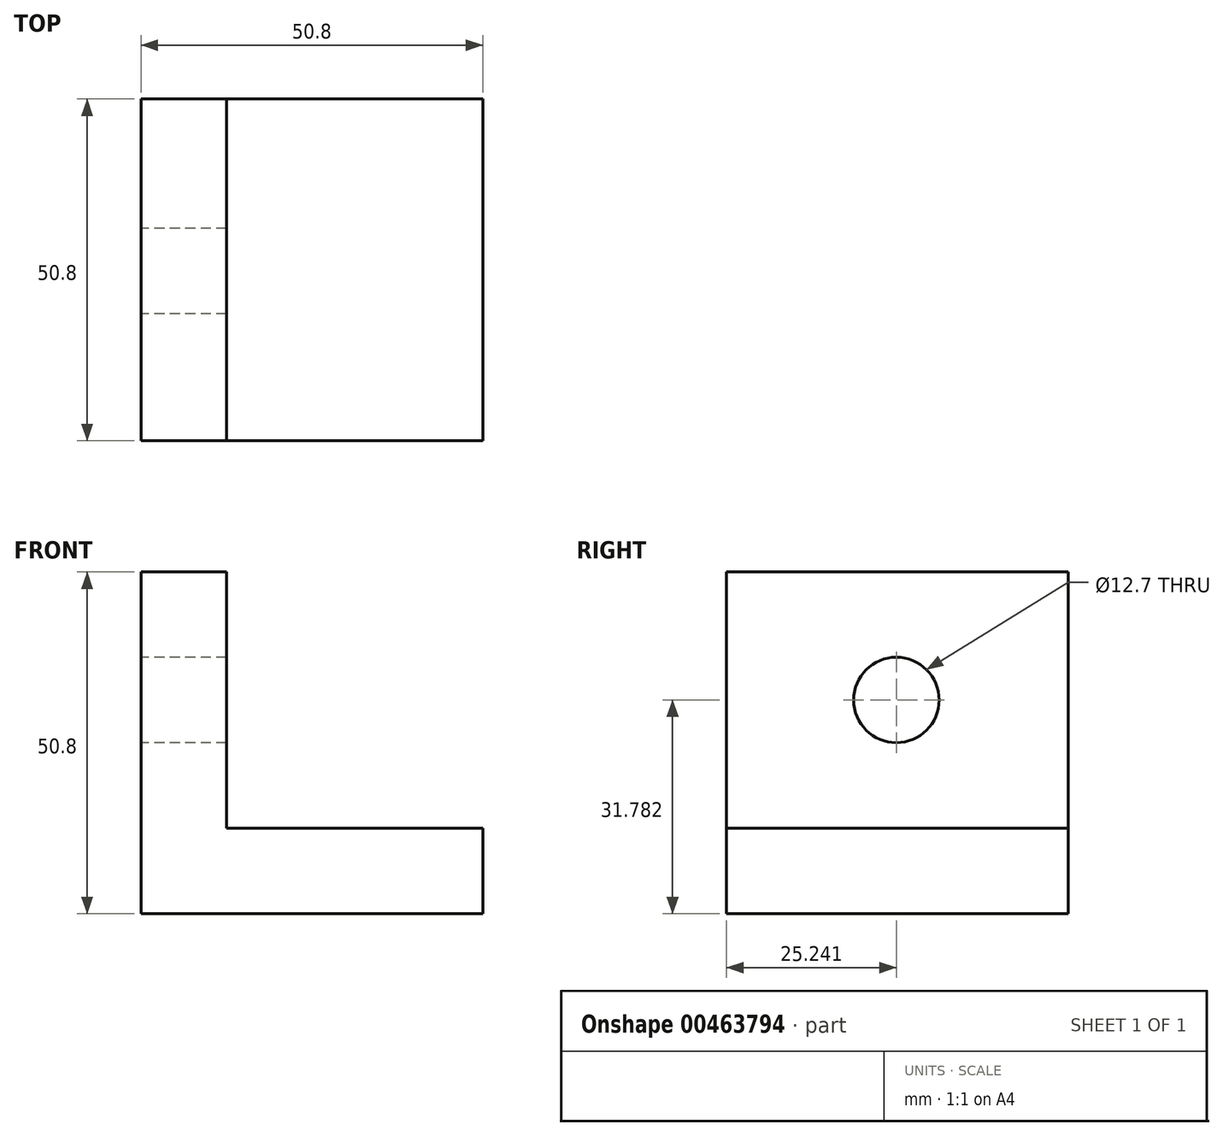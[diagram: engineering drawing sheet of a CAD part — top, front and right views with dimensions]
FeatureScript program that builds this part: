
annotation { "Feature Type Name" : "Feature", "Feature Type Description" : "" }
export const myFeature = defineFeature(function(context is Context, id is Id, definition is map)
    precondition{}
    {
        {
            var Q0;
            Q0=qCreatedBy(makeId("Front.planeOp"),FACE);
            var sketch = newSketch(context, id + "F0", { "sketchPlane" : qUnion([Q0])});
            skLineSegment(sketch, "E0", {"start": v(0, 50.8) * mm, "end": v(0, 0) * mm});
            skLineSegment(sketch, "E1", {"start": v(0, 0) * mm, "end": v(50.8, 0) * mm});
            skLineSegment(sketch, "E2", {"start": v(50.8, 0) * mm, "end": v(50.8, 12.7) * mm});
            skLineSegment(sketch, "E3", {"start": v(50.8, 12.7) * mm, "end": v(12.7, 12.7) * mm});
            skLineSegment(sketch, "E4", {"start": v(12.7, 12.7) * mm, "end": v(12.7, 50.8) * mm});
            skLineSegment(sketch, "E5", {"start": v(12.7, 50.8) * mm, "end": v(0, 50.8) * mm});
            skSolve(sketch);
        }
        {
            var Q0;
            Q0 = qSketchRegion(id + "F0", true);
            extrude(context, id + "F1", {"entities" : qUnion([Q0]), "depth" : 50.8 * mm});
        }
        {
            var Q0;
            Q0=qCreatedBy(makeId("Right.planeOp"),FACE);
            var sketch = newSketch(context, id + "F2", { "sketchPlane" : qUnion([Q0])});
            skCircle(sketch, "E6", {"center": v(-25.56, 31.78) * mm, "radius": 6.35 * mm});
            skSolve(sketch);
        }
        {
            var Q0;
            Q0=sQuery(id+"F2.wireOp",VERTEX,"E6.center");
            var Q1;
            Q1=makeQuery(id+"F1.opExtrude","SWEPT_BODY",BODY,{"disambiguationData":[OSD([sQuery(id+"F0.wireOp",EDGE,"E0"),sQuery(id+"F0.wireOp",EDGE,"E1"),sQuery(id+"F0.wireOp",EDGE,"E2"),sQuery(id+"F0.wireOp",EDGE,"E3"),sQuery(id+"F0.wireOp",EDGE,"E4"),sQuery(id+"F0.wireOp",EDGE,"E5")])]});
            hole(context, id + "F3", {"style" : HoleStyle.SIMPLE, "endStyle" : HoleEndStyle.THROUGH, "oppositeDirection" : true, "holeDiameter" : 12.7 * mm, "isTappedThrough" : true, "tappedDepth" : 12.7 * mm, "tapClearance" : 3, "locations" : qUnion([Q0]), "scope" : qUnion([Q1])});
        }
    });
